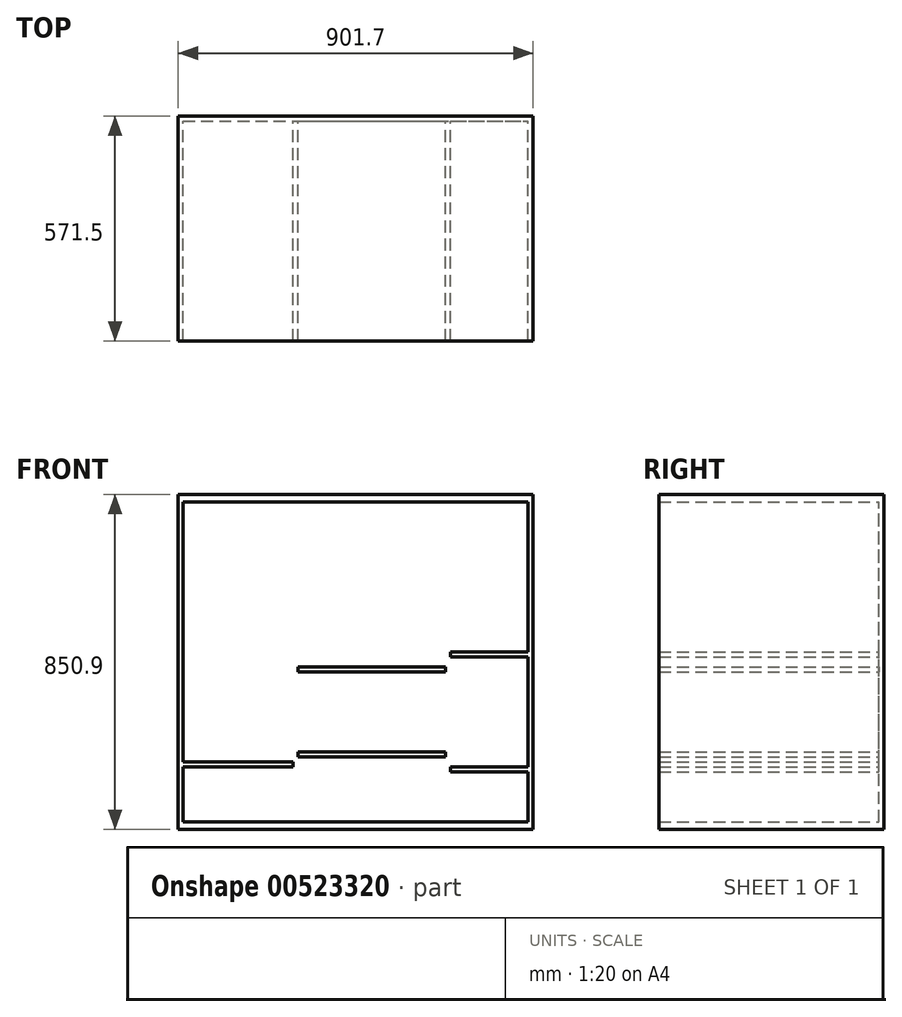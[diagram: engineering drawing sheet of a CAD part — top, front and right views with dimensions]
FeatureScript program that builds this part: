
annotation { "Feature Type Name" : "Feature", "Feature Type Description" : "" }
export const myFeature = defineFeature(function(context is Context, id is Id, definition is map)
    precondition{}
    {
        {
            var Q0;
            Q0=qCreatedBy(makeId("Front.planeOp"),FACE);
            var sketch = newSketch(context, id + "F0", { "sketchPlane" : qUnion([Q0])});
            skLineSegment(sketch, "E0.bottom", {"start": v(0, 0) * mm, "end": v(901.7, 0) * mm});
            skLineSegment(sketch, "E0.top", {"start": v(0, 19.05) * mm, "end": v(901.7, 19.05) * mm});
            skLineSegment(sketch, "E0.left", {"start": v(0, 0) * mm, "end": v(0, 19.05) * mm});
            skLineSegment(sketch, "E0.right", {"start": v(901.7, 0) * mm, "end": v(901.7, 19.05) * mm});
            skLineSegment(sketch, "E1.bottom", {"start": v(0, 19.05) * mm, "end": v(12.7, 19.05) * mm});
            skLineSegment(sketch, "E1.top", {"start": v(0, 831.85) * mm, "end": v(12.7, 831.85) * mm});
            skLineSegment(sketch, "E1.left", {"start": v(0, 19.05) * mm, "end": v(0, 831.85) * mm});
            skLineSegment(sketch, "E1.right", {"start": v(12.7, 19.05) * mm, "end": v(12.7, 831.85) * mm});
            skLineSegment(sketch, "E2.bottom", {"start": v(901.7, 19.05) * mm, "end": v(889, 19.05) * mm});
            skLineSegment(sketch, "E2.top", {"start": v(901.7, 831.85) * mm, "end": v(889, 831.85) * mm});
            skLineSegment(sketch, "E2.left", {"start": v(901.7, 19.05) * mm, "end": v(901.7, 831.85) * mm});
            skLineSegment(sketch, "E2.right", {"start": v(889, 19.05) * mm, "end": v(889, 831.85) * mm});
            skLineSegment(sketch, "E3.bottom", {"start": v(0, 831.85) * mm, "end": v(901.7, 831.85) * mm});
            skLineSegment(sketch, "E3.top", {"start": v(0, 850.9) * mm, "end": v(901.7, 850.9) * mm});
            skLineSegment(sketch, "E3.left", {"start": v(0, 831.85) * mm, "end": v(0, 850.9) * mm});
            skLineSegment(sketch, "E3.right", {"start": v(901.7, 831.85) * mm, "end": v(901.7, 850.9) * mm});
            skLineSegment(sketch, "E4.bottom", {"start": v(679.45, 19.05) * mm, "end": v(692.15, 19.05) * mm});
            skLineSegment(sketch, "E4.top", {"start": v(679.45, 831.85) * mm, "end": v(692.15, 831.85) * mm});
            skLineSegment(sketch, "E4.left", {"start": v(679.45, 19.05) * mm, "end": v(679.45, 831.85) * mm});
            skLineSegment(sketch, "E4.right", {"start": v(692.15, 19.05) * mm, "end": v(692.15, 831.85) * mm});
            skLineSegment(sketch, "E5.bottom", {"start": v(292.1, 19.05) * mm, "end": v(304.8, 19.05) * mm});
            skLineSegment(sketch, "E5.top", {"start": v(292.1, 400.05) * mm, "end": v(304.8, 400.05) * mm});
            skLineSegment(sketch, "E5.left", {"start": v(292.1, 19.05) * mm, "end": v(292.1, 400.05) * mm});
            skLineSegment(sketch, "E5.right", {"start": v(304.8, 19.05) * mm, "end": v(304.8, 400.05) * mm});
            skLineSegment(sketch, "E6.bottom", {"start": v(12.7, 400.05) * mm, "end": v(336.55, 400.05) * mm});
            skLineSegment(sketch, "E6.top", {"start": v(12.7, 412.75) * mm, "end": v(336.55, 412.75) * mm});
            skLineSegment(sketch, "E6.left", {"start": v(12.7, 400.05) * mm, "end": v(12.7, 412.75) * mm});
            skLineSegment(sketch, "E6.right", {"start": v(336.55, 400.05) * mm, "end": v(336.55, 412.75) * mm});
            skLineSegment(sketch, "E7.bottom", {"start": v(215.9, 412.75) * mm, "end": v(228.6, 412.75) * mm});
            skLineSegment(sketch, "E7.top", {"start": v(215.9, 831.85) * mm, "end": v(228.6, 831.85) * mm});
            skLineSegment(sketch, "E7.left", {"start": v(215.9, 412.75) * mm, "end": v(215.9, 831.85) * mm});
            skLineSegment(sketch, "E7.right", {"start": v(228.6, 412.75) * mm, "end": v(228.6, 831.85) * mm});
            skLineSegment(sketch, "E8.bottom", {"start": v(304.8, 196.85) * mm, "end": v(679.45, 196.85) * mm});
            skLineSegment(sketch, "E8.top", {"start": v(304.8, 184.15) * mm, "end": v(679.45, 184.15) * mm});
            skLineSegment(sketch, "E8.left", {"start": v(304.8, 196.85) * mm, "end": v(304.8, 184.15) * mm});
            skLineSegment(sketch, "E8.right", {"start": v(679.45, 196.85) * mm, "end": v(679.45, 184.15) * mm});
            skLineSegment(sketch, "E9.bottom", {"start": v(304.8, 412.75) * mm, "end": v(679.45, 412.75) * mm});
            skLineSegment(sketch, "E9.top", {"start": v(304.8, 400.05) * mm, "end": v(679.45, 400.05) * mm});
            skLineSegment(sketch, "E9.left", {"start": v(304.8, 412.75) * mm, "end": v(304.8, 400.05) * mm});
            skLineSegment(sketch, "E9.right", {"start": v(679.45, 412.75) * mm, "end": v(679.45, 400.05) * mm});
            skLineSegment(sketch, "E10.bottom", {"start": v(336.55, 412.75) * mm, "end": v(349.25, 412.75) * mm});
            skLineSegment(sketch, "E10.top", {"start": v(336.55, 831.85) * mm, "end": v(349.25, 831.85) * mm});
            skLineSegment(sketch, "E10.left", {"start": v(336.55, 412.75) * mm, "end": v(336.55, 831.85) * mm});
            skLineSegment(sketch, "E10.right", {"start": v(349.25, 412.75) * mm, "end": v(349.25, 831.85) * mm});
            skLineSegment(sketch, "E11.bottom", {"start": v(476.25, 412.75) * mm, "end": v(488.95, 412.75) * mm});
            skLineSegment(sketch, "E11.top", {"start": v(476.25, 831.85) * mm, "end": v(488.95, 831.85) * mm});
            skLineSegment(sketch, "E11.left", {"start": v(476.25, 412.75) * mm, "end": v(476.25, 831.85) * mm});
            skLineSegment(sketch, "E11.right", {"start": v(488.95, 412.75) * mm, "end": v(488.95, 831.85) * mm});
            skLineSegment(sketch, "E12.bottom", {"start": v(603.25, 412.75) * mm, "end": v(615.95, 412.75) * mm});
            skLineSegment(sketch, "E12.top", {"start": v(603.25, 831.85) * mm, "end": v(615.95, 831.85) * mm});
            skLineSegment(sketch, "E12.left", {"start": v(603.25, 412.75) * mm, "end": v(603.25, 831.85) * mm});
            skLineSegment(sketch, "E12.right", {"start": v(615.95, 412.75) * mm, "end": v(615.95, 831.85) * mm});
            skLineSegment(sketch, "E13.bottom", {"start": v(692.15, 158.75) * mm, "end": v(889, 158.75) * mm});
            skLineSegment(sketch, "E13.top", {"start": v(692.15, 146.05) * mm, "end": v(889, 146.05) * mm});
            skLineSegment(sketch, "E13.left", {"start": v(692.15, 158.75) * mm, "end": v(692.15, 146.05) * mm});
            skLineSegment(sketch, "E13.right", {"start": v(889, 158.75) * mm, "end": v(889, 146.05) * mm});
            skLineSegment(sketch, "E14.bottom", {"start": v(692.15, 450.85) * mm, "end": v(889, 450.85) * mm});
            skLineSegment(sketch, "E14.top", {"start": v(692.15, 438.15) * mm, "end": v(889, 438.15) * mm});
            skLineSegment(sketch, "E14.left", {"start": v(692.15, 450.85) * mm, "end": v(692.15, 438.15) * mm});
            skLineSegment(sketch, "E14.right", {"start": v(889, 450.85) * mm, "end": v(889, 438.15) * mm});
            skLineSegment(sketch, "E15.bottom", {"start": v(387.35, 196.85) * mm, "end": v(400.05, 196.85) * mm});
            skLineSegment(sketch, "E15.top", {"start": v(387.35, 400.05) * mm, "end": v(400.05, 400.05) * mm});
            skLineSegment(sketch, "E15.left", {"start": v(387.35, 196.85) * mm, "end": v(387.35, 400.05) * mm});
            skLineSegment(sketch, "E15.right", {"start": v(400.05, 196.85) * mm, "end": v(400.05, 400.05) * mm});
            skLineSegment(sketch, "E16.bottom", {"start": v(12.7, 171.45) * mm, "end": v(292.1, 171.45) * mm});
            skLineSegment(sketch, "E16.top", {"start": v(12.7, 158.75) * mm, "end": v(292.1, 158.75) * mm});
            skLineSegment(sketch, "E16.left", {"start": v(12.7, 171.45) * mm, "end": v(12.7, 158.75) * mm});
            skLineSegment(sketch, "E16.right", {"start": v(292.1, 171.45) * mm, "end": v(292.1, 158.75) * mm});
            skSolve(sketch);
        }
        {
            var Q0;
            Q0 = qSketchRegion(id + "F0", true);
            var Q1;
            Q1=makeQuery(id+"F0.imprint","IMPRINT",FACE,{"disambiguationData":[TD([[makeQuery(id+"F0.imprint","IMPRINT",EDGE,{"derivedFrom":sQuery(id+"F0.wireOp",EDGE,"E7.bottom")}),1.0]])]});
            var Q2;
            Q2=makeQuery(id+"F0.imprint","IMPRINT",FACE,{"disambiguationData":[TD([[makeQuery(id+"F0.imprint","IMPRINT",EDGE,{"derivedFrom":sQuery(id+"F0.wireOp",EDGE,"E10.bottom")}),1.0]])]});
            var Q3;
            Q3=makeQuery(id+"F0.imprint","IMPRINT",FACE,{"disambiguationData":[TD([[makeQuery(id+"F0.imprint","IMPRINT",EDGE,{"derivedFrom":sQuery(id+"F0.wireOp",EDGE,"E11.bottom")}),1.0]])]});
            var Q4;
            Q4=makeQuery(id+"F0.imprint","IMPRINT",FACE,{"disambiguationData":[TD([[makeQuery(id+"F0.imprint","IMPRINT",EDGE,{"derivedFrom":sQuery(id+"F0.wireOp",EDGE,"E12.bottom")}),1.0]])]});
            var Q5;
            {var subQ8=sQuery(id+"F0.wireOp",EDGE,"E4.bottom");Q5=makeQuery(id+"F0.imprint","IMPRINT",FACE,{"disambiguationData":[TD([[makeQuery(id+"F0.imprint","IMPRINT",EDGE,{"derivedFrom":subQ8}),1.0]])]});}
            var Q6;
            Q6=makeQuery(id+"F0.imprint","IMPRINT",FACE,{"disambiguationData":[TD([[makeQuery(id+"F0.imprint","IMPRINT",EDGE,{"derivedFrom":sQuery(id+"F0.wireOp",EDGE,"E14.bottom")}),-1.0]])]});
            var Q7;
            Q7=makeQuery(id+"F0.imprint","IMPRINT",FACE,{"disambiguationData":[TD([[makeQuery(id+"F0.imprint","IMPRINT",EDGE,{"derivedFrom":sQuery(id+"F0.wireOp",EDGE,"E13.bottom")}),-1.0]])]});
            var Q8;
            Q8=makeQuery(id+"F0.imprint","IMPRINT",FACE,{"disambiguationData":[TD([[makeQuery(id+"F0.imprint","IMPRINT",EDGE,{"derivedFrom":sQuery(id+"F0.wireOp",EDGE,"E8.top")}),1.0]])]});
            var Q9;
            {var subQ6=sQuery(id+"F0.wireOp",EDGE,"E6.right");Q9=makeQuery(id+"F0.imprint","IMPRINT",FACE,{"disambiguationData":[TD([[makeQuery(id+"F0.imprint","IMPRINT",EDGE,{"derivedFrom":subQ6}),-1.0]])]});}
            var Q10;
            Q10=makeQuery(id+"F0.imprint","IMPRINT",FACE,{"disambiguationData":[TD([[makeQuery(id+"F0.imprint","IMPRINT",EDGE,{"derivedFrom":sQuery(id+"F0.wireOp",EDGE,"E15.bottom")}),1.0]])]});
            var Q11;
            {var subQ0=sQuery(id+"F0.wireOp",EDGE,"E6.right");Q11=makeQuery(id+"F0.imprint","IMPRINT",FACE,{"disambiguationData":[TD([[makeQuery(id+"F0.imprint","IMPRINT",EDGE,{"derivedFrom":subQ0}),1.0]])]});}
            var Q12;
            {var subQ3=sQuery(id+"F0.wireOp",EDGE,"E6.left");Q12=makeQuery(id+"F0.imprint","IMPRINT",FACE,{"disambiguationData":[TD([[makeQuery(id+"F0.imprint","IMPRINT",EDGE,{"derivedFrom":subQ3}),-1.0]])]});}
            var Q13;
            {var subQ1=sQuery(id+"F0.wireOp",EDGE,"E5.bottom");Q13=makeQuery(id+"F0.imprint","IMPRINT",FACE,{"disambiguationData":[TD([[makeQuery(id+"F0.imprint","IMPRINT",EDGE,{"derivedFrom":subQ1}),1.0]])]});}
            var Q14;
            Q14=makeQuery(id+"F0.imprint","IMPRINT",FACE,{"disambiguationData":[TD([[makeQuery(id+"F0.imprint","IMPRINT",EDGE,{"derivedFrom":sQuery(id+"F0.wireOp",EDGE,"E16.bottom")}),-1.0]])]});
            extrude(context, id + "F1", {"entities" : qUnion([Q0, Q1, Q2, Q3, Q4, Q5, Q6, Q7, Q8, Q9, Q10, Q11, Q12, Q13, Q14]), "depth" : 558.8 * mm, "offsetDistance" : 25.4 * mm});
        }
        {
            var Q0;
            Q0=makeQuery(id+"F1.opExtrude","CAP_FACE",FACE,{"disambiguationData":[OSD([sQuery(id+"F0.wireOp",EDGE,"E0.bottom"),sQuery(id+"F0.wireOp",EDGE,"E0.top"),sQuery(id+"F0.wireOp",EDGE,"E0.left"),sQuery(id+"F0.wireOp",EDGE,"E0.right"),sQuery(id+"F0.wireOp",EDGE,"E1.left"),sQuery(id+"F0.wireOp",EDGE,"E1.right"),sQuery(id+"F0.wireOp",EDGE,"E2.left"),sQuery(id+"F0.wireOp",EDGE,"E2.right"),sQuery(id+"F0.wireOp",EDGE,"E3.bottom"),sQuery(id+"F0.wireOp",EDGE,"E3.top"),sQuery(id+"F0.wireOp",EDGE,"E3.left"),sQuery(id+"F0.wireOp",EDGE,"E3.right"),sQuery(id+"F0.wireOp",EDGE,"E4.left"),sQuery(id+"F0.wireOp",EDGE,"E4.right"),sQuery(id+"F0.wireOp",EDGE,"E5.left"),sQuery(id+"F0.wireOp",EDGE,"E5.right"),sQuery(id+"F0.wireOp",EDGE,"E6.bottom"),sQuery(id+"F0.wireOp",EDGE,"E6.top"),sQuery(id+"F0.wireOp",EDGE,"E7.left"),sQuery(id+"F0.wireOp",EDGE,"E7.right"),sQuery(id+"F0.wireOp",EDGE,"E8.bottom"),sQuery(id+"F0.wireOp",EDGE,"E8.top"),sQuery(id+"F0.wireOp",EDGE,"E9.bottom"),sQuery(id+"F0.wireOp",EDGE,"E9.top"),sQuery(id+"F0.wireOp",EDGE,"E10.left"),sQuery(id+"F0.wireOp",EDGE,"E10.right"),sQuery(id+"F0.wireOp",EDGE,"E11.left"),sQuery(id+"F0.wireOp",EDGE,"E11.right"),sQuery(id+"F0.wireOp",EDGE,"E12.left"),sQuery(id+"F0.wireOp",EDGE,"E12.right"),sQuery(id+"F0.wireOp",EDGE,"E13.bottom"),sQuery(id+"F0.wireOp",EDGE,"E13.top"),sQuery(id+"F0.wireOp",EDGE,"E14.bottom"),sQuery(id+"F0.wireOp",EDGE,"E14.top"),sQuery(id+"F0.wireOp",EDGE,"E15.left"),sQuery(id+"F0.wireOp",EDGE,"E15.right"),sQuery(id+"F0.wireOp",EDGE,"E16.bottom"),sQuery(id+"F0.wireOp",EDGE,"E16.top")])],"isStart":true});
            var sketch = newSketch(context, id + "F2", { "sketchPlane" : qUnion([Q0])});
            skLineSegment(sketch, "E17.bottom", {"start": v(-901.7, 0) * mm, "end": v(0, 0) * mm});
            skLineSegment(sketch, "E17.top", {"start": v(-901.7, 850.9) * mm, "end": v(0, 850.9) * mm});
            skLineSegment(sketch, "E17.left", {"start": v(-901.7, 0) * mm, "end": v(-901.7, 850.9) * mm});
            skLineSegment(sketch, "E17.right", {"start": v(0, 0) * mm, "end": v(0, 850.9) * mm});
            skSolve(sketch);
        }
        {
            var Q0;
            Q0 = qSketchRegion(id + "F2", true);
            extrude(context, id + "F3", {"entities" : qUnion([Q0]), "operationType" : NewBodyOperationType.ADD, "depth" : 12.7 * mm, "offsetDistance" : 25.4 * mm});
        }
    });
